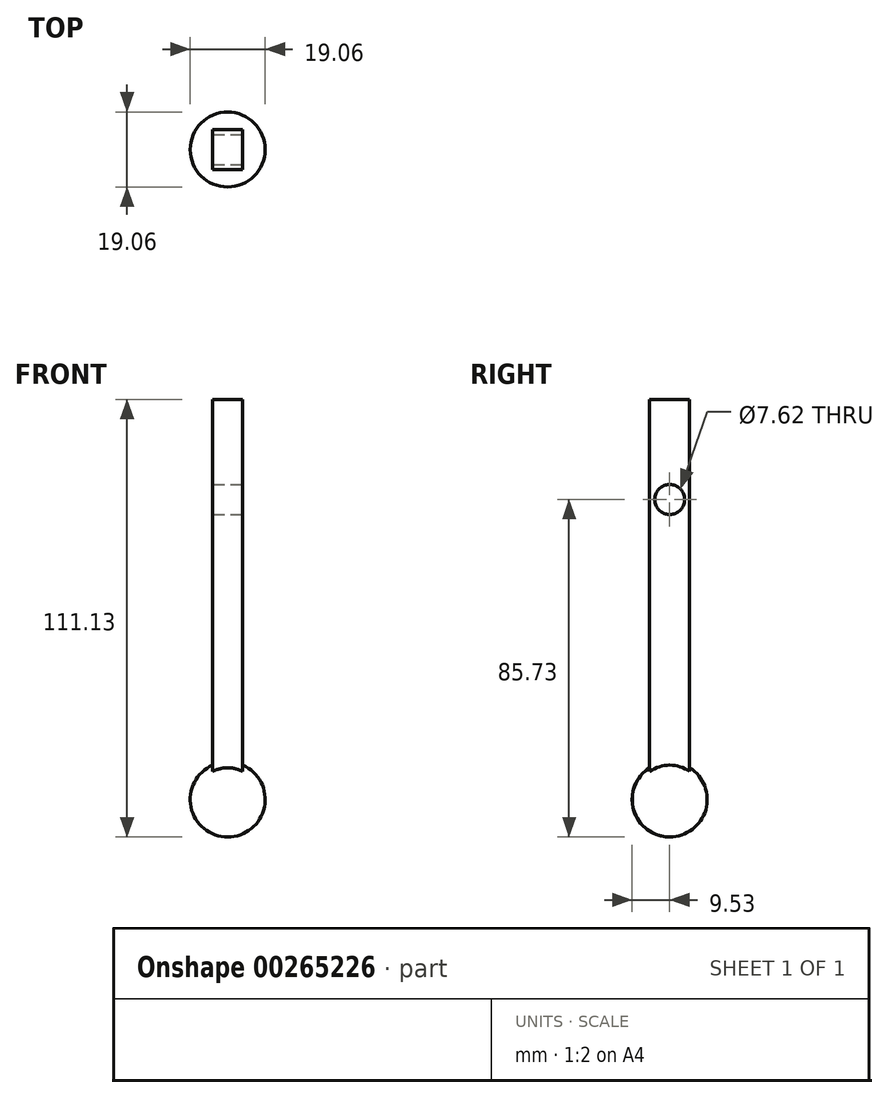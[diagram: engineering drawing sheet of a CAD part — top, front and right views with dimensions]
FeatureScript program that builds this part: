
annotation { "Feature Type Name" : "Feature", "Feature Type Description" : "" }
export const myFeature = defineFeature(function(context is Context, id is Id, definition is map)
    precondition{}
    {
        {
            var Q0;
            Q0=qCreatedBy(makeId("Right.planeOp"),FACE);
            var sketch = newSketch(context, id + "F0", { "sketchPlane" : qUnion([Q0])});
            skLineSegment(sketch, "E0", {"start": v(0, -9.53) * mm, "end": v(0, 9.53) * mm});
            skArc(sketch, "E1", {"start": v(0, -9.53) * mm, "mid": v(-9.53, 0) * mm, "end": v(0, 9.53) * mm});
            skSolve(sketch);
        }
        {
            var Q0;
            Q0=makeQuery(id+"F0.imprint","IMPRINT",FACE,{"disambiguationData":[TD([[makeQuery(id+"F0.imprint","IMPRINT",EDGE,{"derivedFrom":sQuery(id+"F0.wireOp",EDGE,"E0")}),1.0]])]});
            var Q1;
            Q1=sQuery(id+"F0.wireOp",EDGE,"E0");
            revolve(context, id + "F1", {"entities" : qUnion([Q0]), "axis" : qUnion([Q1]), "revolveType" : RevolveType.FULL});
        }
        {
            var Q0;
            Q0=qCreatedBy(makeId("Top.planeOp"),FACE);
            var sketch = newSketch(context, id + "F2", { "sketchPlane" : qUnion([Q0])});
            skLineSegment(sketch, "E2.bottom", {"start": v(-3.8, 5.08) * mm, "end": v(3.8, 5.08) * mm});
            skLineSegment(sketch, "E2.top", {"start": v(-3.8, -5.08) * mm, "end": v(3.8, -5.08) * mm});
            skLineSegment(sketch, "E2.left", {"start": v(-3.81, 5.08) * mm, "end": v(-3.81, -5.08) * mm});
            skLineSegment(sketch, "E2.right", {"start": v(3.81, 5.08) * mm, "end": v(3.81, -5.08) * mm});
            skPoint(sketch, "E2.middle", {"position": v(0, 0) * mm});
            skSolve(sketch);
        }
        {
            var Q0;
            Q0 = qSketchRegion(id + "F2", true);
            extrude(context, id + "F3", {"entities" : qUnion([Q0]), "operationType" : NewBodyOperationType.ADD, "depth" : 101.6 * mm});
        }
        {
            var Q0;
            Q0=qCreatedBy(makeId("Right.planeOp"),FACE);
            var sketch = newSketch(context, id + "F4", { "sketchPlane" : qUnion([Q0])});
            skCircle(sketch, "E3", {"center": v(0, 76.2) * mm, "radius": 3.81 * mm});
            skSolve(sketch);
        }
        {
            var Q0;
            Q0 = qSketchRegion(id + "F4", true);
            extrude(context, id + "F5", {"entities" : qUnion([Q0]), "operationType" : NewBodyOperationType.REMOVE, "endBound" : BoundingType.THROUGH_ALL, "oppositeDirection" : true, "depth" : 25.4 * mm, "hasSecondDirection" : true, "secondDirectionBound" : SecondDirectionBoundingType.THROUGH_ALL, "secondDirectionOppositeDirection" : false, "secondDirectionDepth" : 25.4 * mm});
        }
    });
